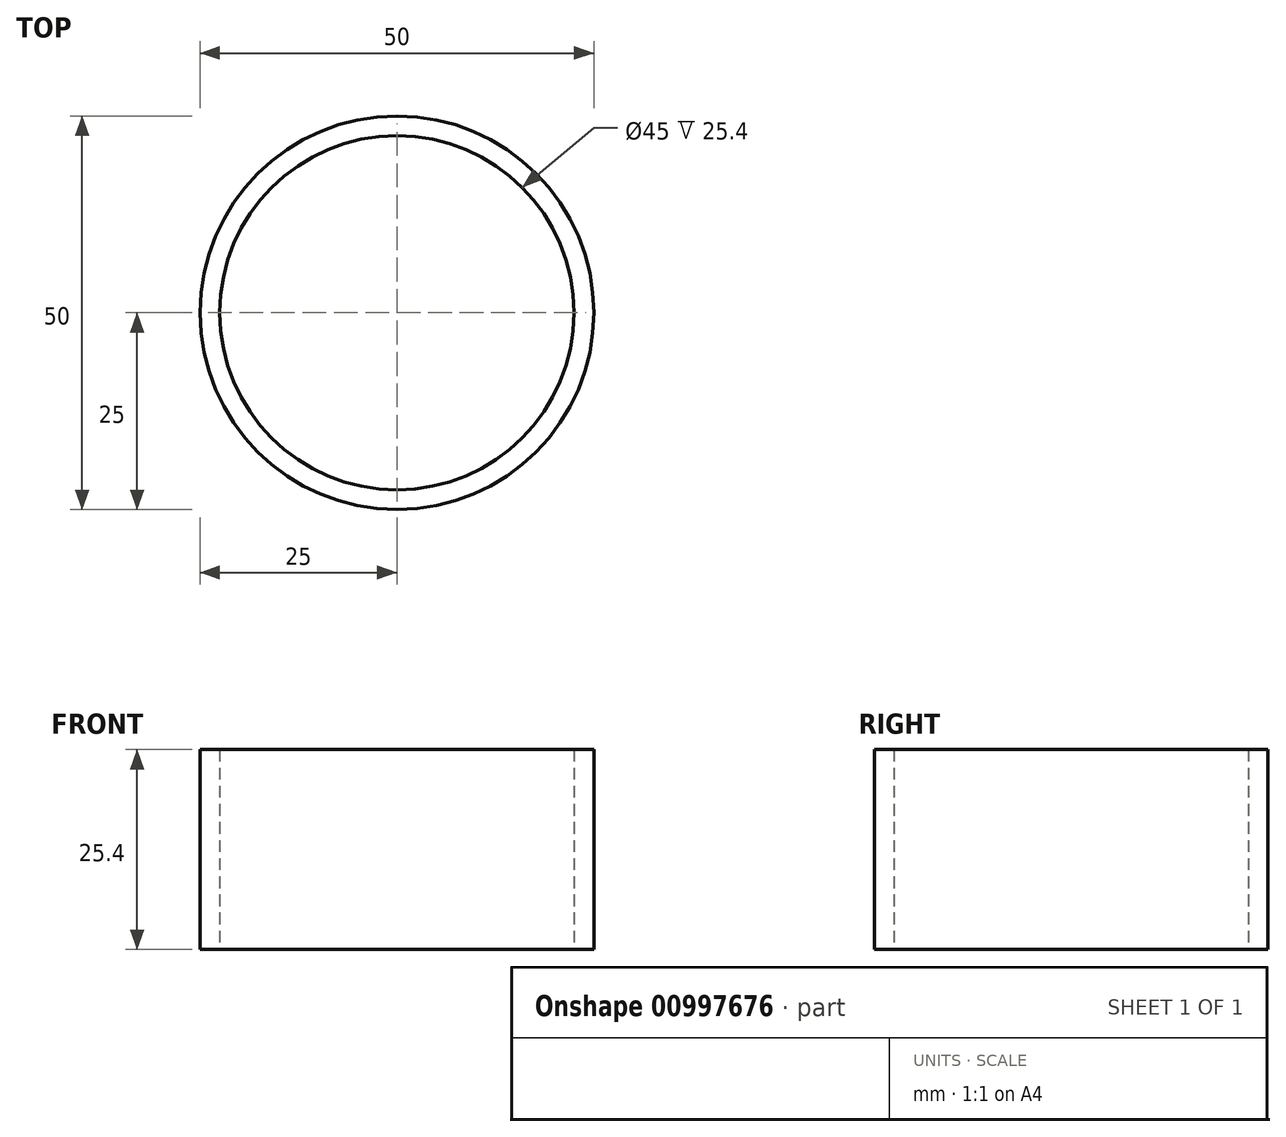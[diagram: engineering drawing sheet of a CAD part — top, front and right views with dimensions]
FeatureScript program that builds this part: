
annotation { "Feature Type Name" : "Feature", "Feature Type Description" : "" }
export const myFeature = defineFeature(function(context is Context, id is Id, definition is map)
    precondition{}
    {
        {
            var Q0;
            Q0=qCreatedBy(makeId("Top.planeOp"),FACE);
            var sketch = newSketch(context, id + "F0", { "sketchPlane" : qUnion([Q0])});
            skCircle(sketch, "E0", {"center": v(0, 0) * mm, "radius": 22.5 * mm});
            skCircle(sketch, "E1", {"center": v(0, 0) * mm, "radius": 25 * mm});
            skSolve(sketch);
        }
        {
            var Q0;
            Q0 = qSketchRegion(id + "F0", true);
            extrude(context, id + "F1", {"entities" : qUnion([Q0]), "depth" : 25.4 * mm, "offsetDistance" : 25.4 * mm});
        }
    });
